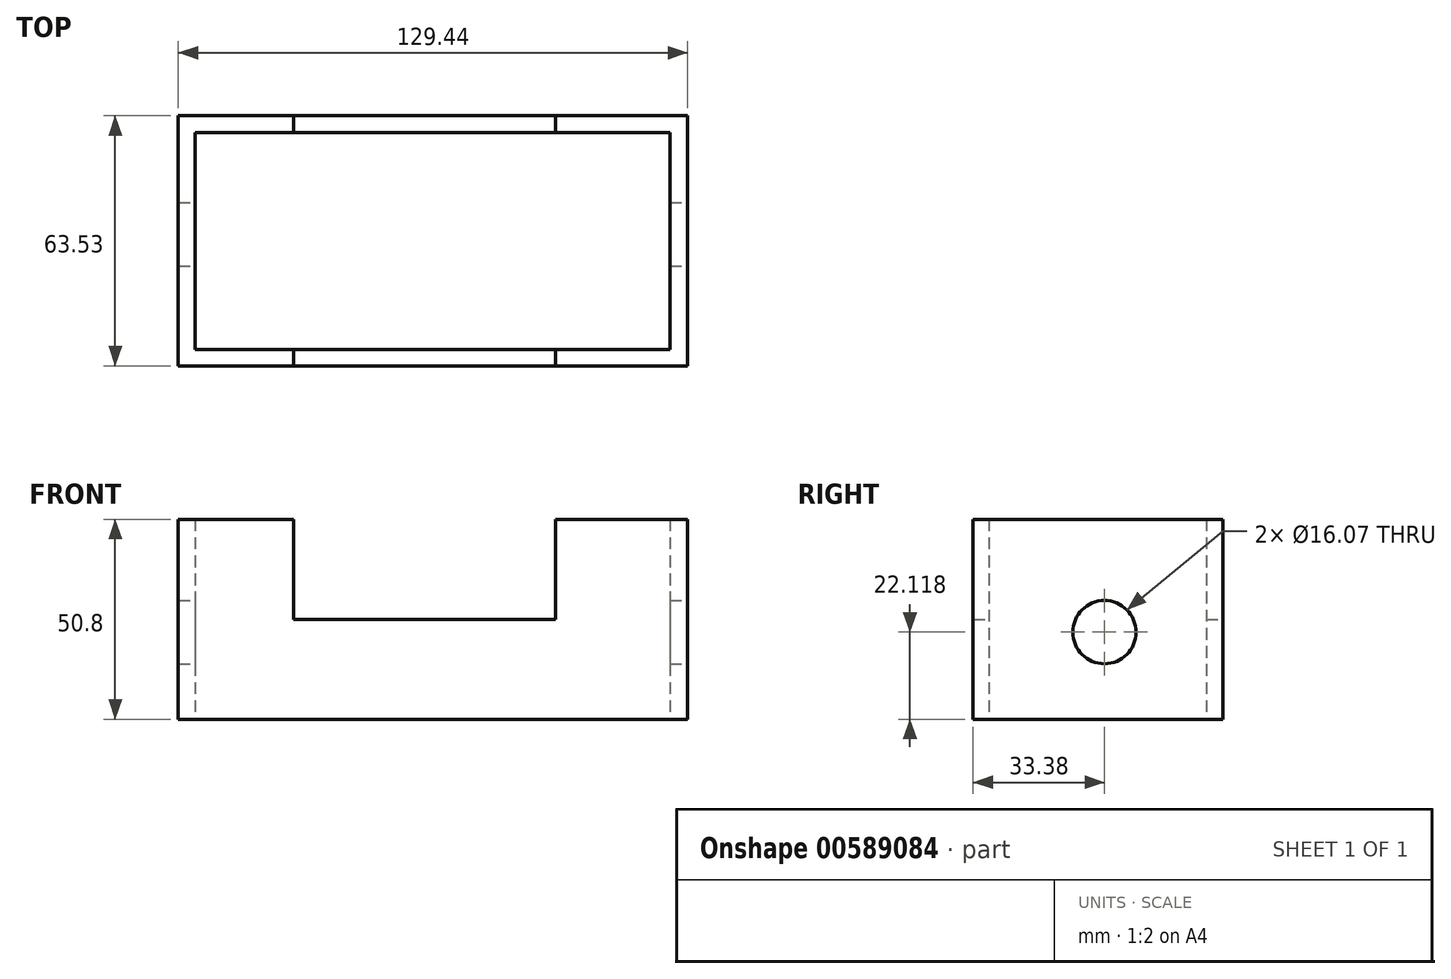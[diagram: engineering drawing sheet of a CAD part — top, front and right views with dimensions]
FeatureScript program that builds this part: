
annotation { "Feature Type Name" : "Feature", "Feature Type Description" : "" }
export const myFeature = defineFeature(function(context is Context, id is Id, definition is map)
    precondition{}
    {
        {
            var Q0;
            Q0=qCreatedBy(makeId("Top.planeOp"),FACE);
            var sketch = newSketch(context, id + "F0", { "sketchPlane" : qUnion([Q0])});
            skLineSegment(sketch, "E0.bottom", {"start": v(-62.78, -33.38) * mm, "end": v(66.66, -33.38) * mm});
            skLineSegment(sketch, "E0.top", {"start": v(-62.78, 30.15) * mm, "end": v(66.66, 30.15) * mm});
            skLineSegment(sketch, "E0.left", {"start": v(-62.78, -33.38) * mm, "end": v(-62.78, 30.15) * mm});
            skLineSegment(sketch, "E0.right", {"start": v(66.66, -33.38) * mm, "end": v(66.66, 30.15) * mm});
            skLineSegment(sketch, "E1.bottom", {"start": v(-58.47, -29.3) * mm, "end": v(62.13, -29.3) * mm});
            skLineSegment(sketch, "E1.top", {"start": v(-58.47, 25.84) * mm, "end": v(62.13, 25.84) * mm});
            skLineSegment(sketch, "E1.left", {"start": v(-58.47, -29.3) * mm, "end": v(-58.47, 25.84) * mm});
            skLineSegment(sketch, "E1.right", {"start": v(62.13, -29.3) * mm, "end": v(62.13, 25.84) * mm});
            skLineSegment(sketch, "E2", {"start": v(33.06, -33.38) * mm, "end": v(33.06, -29.3) * mm});
            skLineSegment(sketch, "E3", {"start": v(33.06, 25.84) * mm, "end": v(33.06, 30.15) * mm});
            skLineSegment(sketch, "E4", {"start": v(-33.5, 30.15) * mm, "end": v(-33.5, 25.84) * mm});
            skLineSegment(sketch, "E5", {"start": v(-33.5, -29.3) * mm, "end": v(-33.5, -33.38) * mm});
            skSolve(sketch);
        }
        {
            var Q0;
            {var subQ0=sQuery(id+"F0.wireOp",EDGE,"E2");Q0=makeQuery(id+"F0.imprint","IMPRINT",FACE,{"disambiguationData":[TD([[makeQuery(id+"F0.imprint","IMPRINT",EDGE,{"derivedFrom":subQ0}),1.0]])]});}
            var Q1;
            {var subQ0=sQuery(id+"F0.wireOp",EDGE,"E0.left");Q1=makeQuery(id+"F0.imprint","IMPRINT",FACE,{"disambiguationData":[TD([[makeQuery(id+"F0.imprint","IMPRINT",EDGE,{"derivedFrom":subQ0}),-1.0]])]});}
            var Q2;
            {var subQ0=sQuery(id+"F0.wireOp",EDGE,"E3");Q2=makeQuery(id+"F0.imprint","IMPRINT",FACE,{"disambiguationData":[TD([[makeQuery(id+"F0.imprint","IMPRINT",EDGE,{"derivedFrom":subQ0}),1.0]])]});}
            var Q3;
            {var subQ3=sQuery(id+"F0.wireOp",EDGE,"E0.right");Q3=makeQuery(id+"F0.imprint","IMPRINT",FACE,{"disambiguationData":[TD([[makeQuery(id+"F0.imprint","IMPRINT",EDGE,{"derivedFrom":subQ3}),1.0]])]});}
            extrude(context, id + "F1", {"entities" : qUnion([Q0, Q1, Q2, Q3]), "depth" : 25.4 * mm, "offsetDistance" : 25.4 * mm});
        }
        {
            var Q0;
            {var subQ0=sQuery(id+"F0.wireOp",EDGE,"E0.left");Q0=makeQuery(id+"F0.imprint","IMPRINT",FACE,{"disambiguationData":[TD([[makeQuery(id+"F0.imprint","IMPRINT",EDGE,{"derivedFrom":subQ0}),-1.0]])]});}
            var Q1;
            {var subQ3=sQuery(id+"F0.wireOp",EDGE,"E0.right");Q1=makeQuery(id+"F0.imprint","IMPRINT",FACE,{"disambiguationData":[TD([[makeQuery(id+"F0.imprint","IMPRINT",EDGE,{"derivedFrom":subQ3}),1.0]])]});}
            extrude(context, id + "F2", {"entities" : qUnion([Q0, Q1]), "operationType" : NewBodyOperationType.ADD, "depth" : 50.8 * mm, "offsetDistance" : 25.4 * mm});
        }
        {
            var Q0;
            {var subQ0=sQuery(id+"F0.wireOp",EDGE,"E0.right");Q0=makeQuery(id+"F2.boolean.opBoolean","MERGE",FACE,{"derivedFrom":[makeQuery(id+"F1.opExtrude","SWEPT_FACE",FACE,{"disambiguationData":[OSD([subQ0])]}),makeQuery(id+"F2.opExtrude","SWEPT_FACE",FACE,{"disambiguationData":[OSD([subQ0])]})]});}
            var sketch = newSketch(context, id + "F3", { "sketchPlane" : qUnion([Q0])});
            skCircle(sketch, "E6", {"center": v(0, 22.12) * mm, "radius": 8.03 * mm});
            skSolve(sketch);
        }
        {
            var Q0;
            Q0 = qSketchRegion(id + "F3", true);
            extrude(context, id + "F4", {"entities" : qUnion([Q0]), "operationType" : NewBodyOperationType.REMOVE, "oppositeDirection" : true, "depth" : 131.06 * mm, "offsetDistance" : 25.4 * mm});
        }
    });
